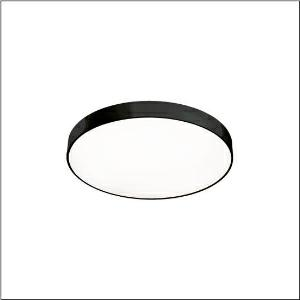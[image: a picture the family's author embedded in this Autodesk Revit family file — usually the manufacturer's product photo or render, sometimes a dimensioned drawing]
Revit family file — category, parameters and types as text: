
# Revit family: round_21_m_51mr36gd0321b
name_source: partatom
category: Lighting Fixtures
units: mm (PartAtom-declared; Revit-internal decimal feet)

## family parameters
Cut with Voids When Loaded = No
Host = Face
Light Source = No
Part Type = Normal
Room Calculation Point = No
Round Connector Dimension = Use Diameter
Shared = No

## types (1)
- Round 21 M (1 x LED, 6840 lm, 54.5 W, 3000K)
    Apparent Load = 55 VA
    CIE Flux Codes = 49 80 96 85 100
    Color Rendering = 80
    Color Temperature = 3000K
    Default Elevation = 1800 mm
    Description = Round 21 M, wall and ceiling luminaire, primary optical cover: cover, of PMMA, opal, light emission: direct/indirect distribution, primary light characteristic: symmetric, installation type: suspended mounting, surface-mounted, LED, rated luminous flux: 6.790lm, luminous efficacy: 124lm/W, light colour: 830, colour temperature: 3000K, with terminal, 5-pole, mains connection: 230V, AC, 50/60Hz, rated input power: 55W, housing, of aluminium, coated, black, diameter: 600mm, height: 62mm, protection rating (complete): IP40, insulation class (complete): insulation class I (protective earthing), certification: CE, impact resistance: IK04, permissible operating ambient temperature: -10..+35°C, packaging unit: 1 piece
    Height = 87 mm
    Lamp = 1 x LED
    Lamp Light Flux = 6840 lm
    Lamp Power = 54.5 W
    Lamp count = 1
    Length = 600 mm
    Luminous efficacy = 126 lm/W
    Manufacturer = Siteco
    ModVariant = No
    Model = 51MR36GD0321B
    Mounting Place = Ceiling
    Mounting Type = Surface mounted
    Number of Poles = 1
    OnlyDefault = Yes
    Power Factor = 1
    Product Name = Round 21 M
    Product group = wall and ceiling luminaire
    ProductGroupID = 302
    Protection Class = Protection class I
    Protection Degree = IP 40
    RLX_Detail_Level = 1
    RLX_Emergency_Light_Flux = 0 lm
    RLX_Emergency_Type = 0
    RLX_Emergency_Type_DB = No
    RlxData = <blob elided: 18101 chars, md5=381e6f6c>
    Socket = socket
    Standby Power = 0 W
    System Light Flux = 6840 lm
    System Power = 55 W
    Type Comments = Product without accessories
    Type Image = l_1258332.jpg
    URL = http://relux.com
    VarID = ---
    Voltage = 0 V
    Weight = 0.00 kg
    Width = 0 mm  [stored 0 ft]

note: [stored X ft] marks values corroborated as IEEE doubles in the binary element streams (Revit-internal decimal feet)

## geometry (parser evidence)
native form markers: Blend x4, Sweep x14
no freeform markers — native parametric forms only
